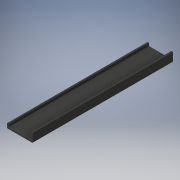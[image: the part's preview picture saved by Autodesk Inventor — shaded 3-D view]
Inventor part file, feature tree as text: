
AUTODESK INVENTOR PART (.ipt)
format: ipt  version: 2019.4 (Build 234330000, 330)  size: 103,936 bytes
history: native  units: mm
features: other x1, extrude x1, sketch x1
ambient origin geometry x8: Origin, YZ Plane, XZ Plane, XY Plane, X Axis, Y Axis, Z Axis, Center Point
bodies: Body1 (feature_tree)
feature tree (3):
  other  "Sólido1"
  extrude  "Extrusão1"  Depth=10.0mm
  sketch  "Esboço1"  dims[d0=180.0mm d1=10.0mm d2=60.0mm d3=10.0mm d4=10.0mm d5=30.0mm d6=1000.0mm d7=0.0mm]
